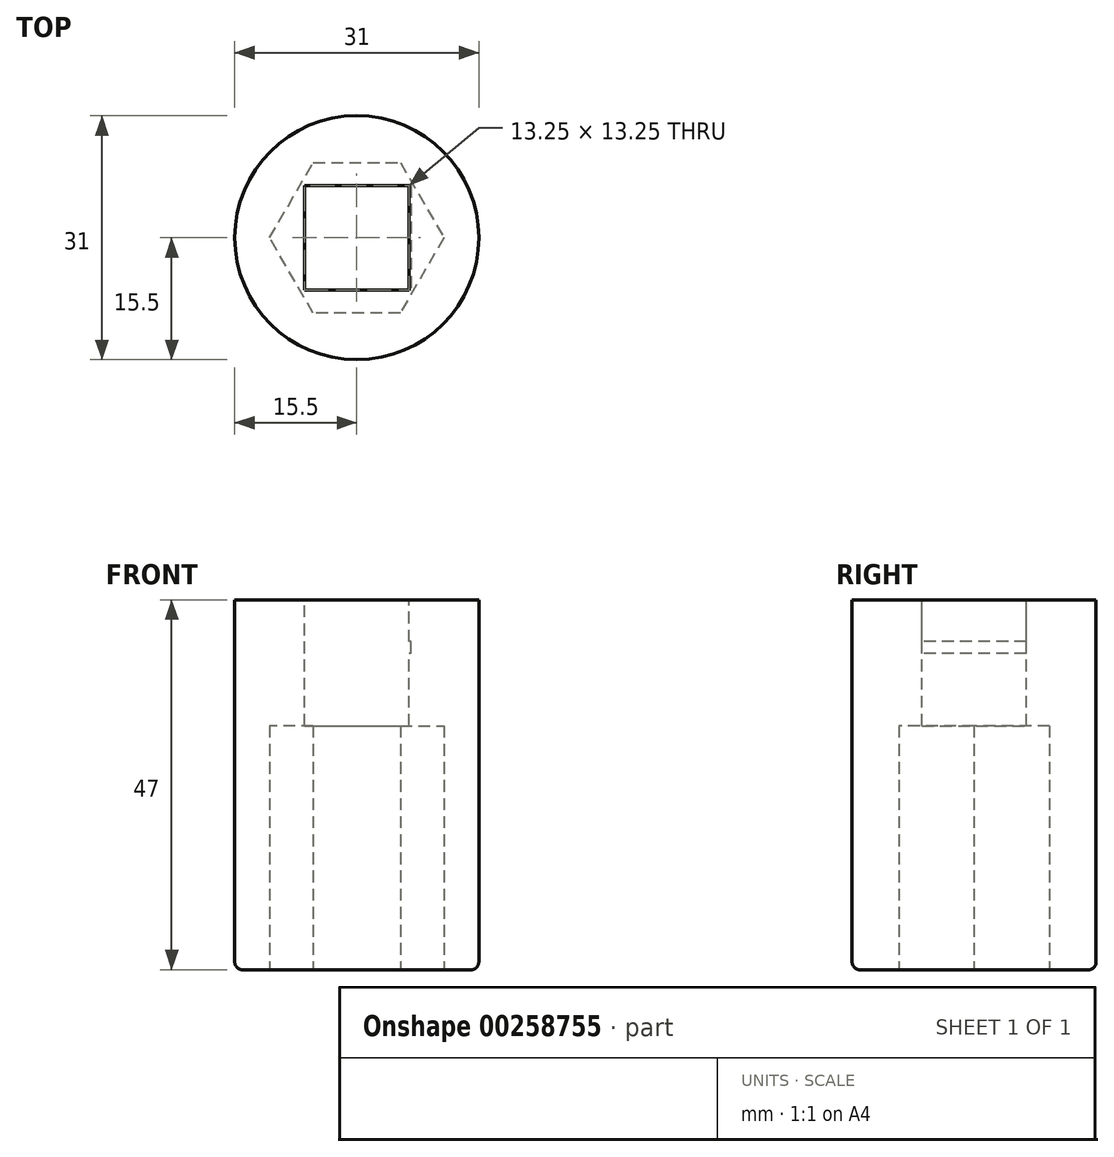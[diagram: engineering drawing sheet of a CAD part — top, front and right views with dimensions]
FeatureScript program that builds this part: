
annotation { "Feature Type Name" : "Feature", "Feature Type Description" : "" }
export const myFeature = defineFeature(function(context is Context, id is Id, definition is map)
    precondition{}
    {
        {
            var Q0;
            Q0=qCreatedBy(makeId("Top.planeOp"),FACE);
            var sketch = newSketch(context, id + "F0", { "sketchPlane" : qUnion([Q0])});
            skCircle(sketch, "E0.cCircle", {"center": v(0, 0) * mm, "radius": 9.57 * mm, "construction": true});
            skLineSegment(sketch, "E0.0", {"start": v(5.53, 9.57) * mm, "end": v(11.06, 0) * mm});
            skLineSegment(sketch, "E0.1", {"start": v(11.06, 0) * mm, "end": v(5.53, -9.58) * mm});
            skLineSegment(sketch, "E0.2", {"start": v(5.53, -9.58) * mm, "end": v(-5.53, -9.57) * mm});
            skLineSegment(sketch, "E0.3", {"start": v(-5.53, -9.57) * mm, "end": v(-11.06, 0) * mm});
            skLineSegment(sketch, "E0.4", {"start": v(-11.06, 0) * mm, "end": v(-5.53, 9.58) * mm});
            skLineSegment(sketch, "E0.5", {"start": v(-5.53, 9.58) * mm, "end": v(5.53, 9.57) * mm});
            skPoint(sketch, "E0.0.midPoint", {"position": v(8.3, 4.79) * mm});
            skCircle(sketch, "E1", {"center": v(0, 0) * mm, "radius": 15.5 * mm});
            skSolve(sketch);
        }
        {
            var Q0;
            Q0=makeQuery(id+"F0.imprint","IMPRINT",FACE,{"disambiguationData":[TD([[makeQuery(id+"F0.imprint","IMPRINT",EDGE,{"derivedFrom":sQuery(id+"F0.wireOp",EDGE,"E0.0")}),1.0]])]});
            extrude(context, id + "F1", {"entities" : qUnion([Q0]), "depth" : 31 * mm});
        }
        {
            var Q0;
            Q0=makeQuery(id+"F1.opExtrude","CAP_FACE",FACE,{"disambiguationData":[OSD([sQuery(id+"F0.wireOp",EDGE,"E0.0"),sQuery(id+"F0.wireOp",EDGE,"E0.1"),sQuery(id+"F0.wireOp",EDGE,"E0.2"),sQuery(id+"F0.wireOp",EDGE,"E0.3"),sQuery(id+"F0.wireOp",EDGE,"E0.4"),sQuery(id+"F0.wireOp",EDGE,"E0.5"),sQuery(id+"F0.wireOp",EDGE,"E1")])],"isStart":false});
            var sketch = newSketch(context, id + "F2", { "sketchPlane" : qUnion([Q0])});
            skCircle(sketch, "E2.0", {"center": v(0, 0) * mm, "radius": 15.5 * mm});
            skSolve(sketch);
        }
        {
            var Q0;
            Q0 = qSketchRegion(id + "F2", true);
            extrude(context, id + "F3", {"entities" : qUnion([Q0]), "operationType" : NewBodyOperationType.ADD, "depth" : 16 * mm});
        }
        {
            var Q0;
            Q0=makeQuery(id+"F3.opExtrude","CAP_FACE",FACE,{"disambiguationData":[OSD([sQuery(id+"F2.wireOp",EDGE,"E2.0")])],"isStart":false});
            var sketch = newSketch(context, id + "F4", { "sketchPlane" : qUnion([Q0])});
            skLineSegment(sketch, "E3.bottom", {"start": v(6.62, 6.63) * mm, "end": v(-6.63, 6.63) * mm});
            skLineSegment(sketch, "E3.top", {"start": v(6.63, -6.63) * mm, "end": v(-6.62, -6.63) * mm});
            skLineSegment(sketch, "E3.left", {"start": v(6.62, 6.63) * mm, "end": v(6.63, -6.63) * mm});
            skLineSegment(sketch, "E3.right", {"start": v(-6.63, 6.63) * mm, "end": v(-6.62, -6.63) * mm});
            skPoint(sketch, "E3.middle", {"position": v(0, 0) * mm});
            skSolve(sketch);
        }
        {
            var Q0;
            Q0=makeQuery(id+"F4.imprint","IMPRINT",FACE,{"disambiguationData":[TD([[makeQuery(id+"F4.imprint","IMPRINT",EDGE,{"derivedFrom":sQuery(id+"F4.wireOp",EDGE,"E3.bottom")}),1.0]])]});
            extrude(context, id + "F5", {"entities" : qUnion([Q0]), "operationType" : NewBodyOperationType.REMOVE, "endBound" : BoundingType.UP_TO_NEXT, "oppositeDirection" : true, "depth" : 25 * mm});
        }
        {
            var Q0;
            Q0=makeQuery(id+"F5.boolean.opBoolean","COPY",FACE,{"derivedFrom":makeQuery(id+"F5.opExtrude","SWEPT_FACE",FACE,{"disambiguationData":[OSD([sQuery(id+"F4.wireOp",EDGE,"E3.left")])]})});
            var sketch = newSketch(context, id + "F6", { "sketchPlane" : qUnion([Q0])});
            skLineSegment(sketch, "E4.bottom", {"start": v(-6.62, 41.7) * mm, "end": v(6.63, 41.7) * mm});
            skLineSegment(sketch, "E4.top", {"start": v(-6.62, 40.2) * mm, "end": v(6.63, 40.2) * mm});
            skLineSegment(sketch, "E4.left", {"start": v(-6.62, 41.7) * mm, "end": v(-6.62, 40.2) * mm});
            skLineSegment(sketch, "E4.right", {"start": v(6.63, 41.7) * mm, "end": v(6.63, 40.2) * mm});
            skSolve(sketch);
        }
        {
            var Q0;
            Q0=makeQuery(id+"F6.imprint","IMPRINT",FACE,{"disambiguationData":[TD([[makeQuery(id+"F6.imprint","IMPRINT",EDGE,{"derivedFrom":sQuery(id+"F6.wireOp",EDGE,"E4.bottom")}),-1.0]])]});
            extrude(context, id + "F7", {"entities" : qUnion([Q0]), "operationType" : NewBodyOperationType.REMOVE, "oppositeDirection" : true, "depth" : .25 * mm});
        }
        {
            var Q0;
            Q0=makeQuery(id+"F1.opExtrude","CAP_EDGE",EDGE,{"disambiguationData":[OSD([sQuery(id+"F0.wireOp",EDGE,"E1")])],"isStart":true});
            fillet(context, id + "F8", {"entities" : qUnion([Q0]), "radius" : 1 * mm, "tangentPropagation" : true, "allowEdgeOverflow" : false});
        }
    });
